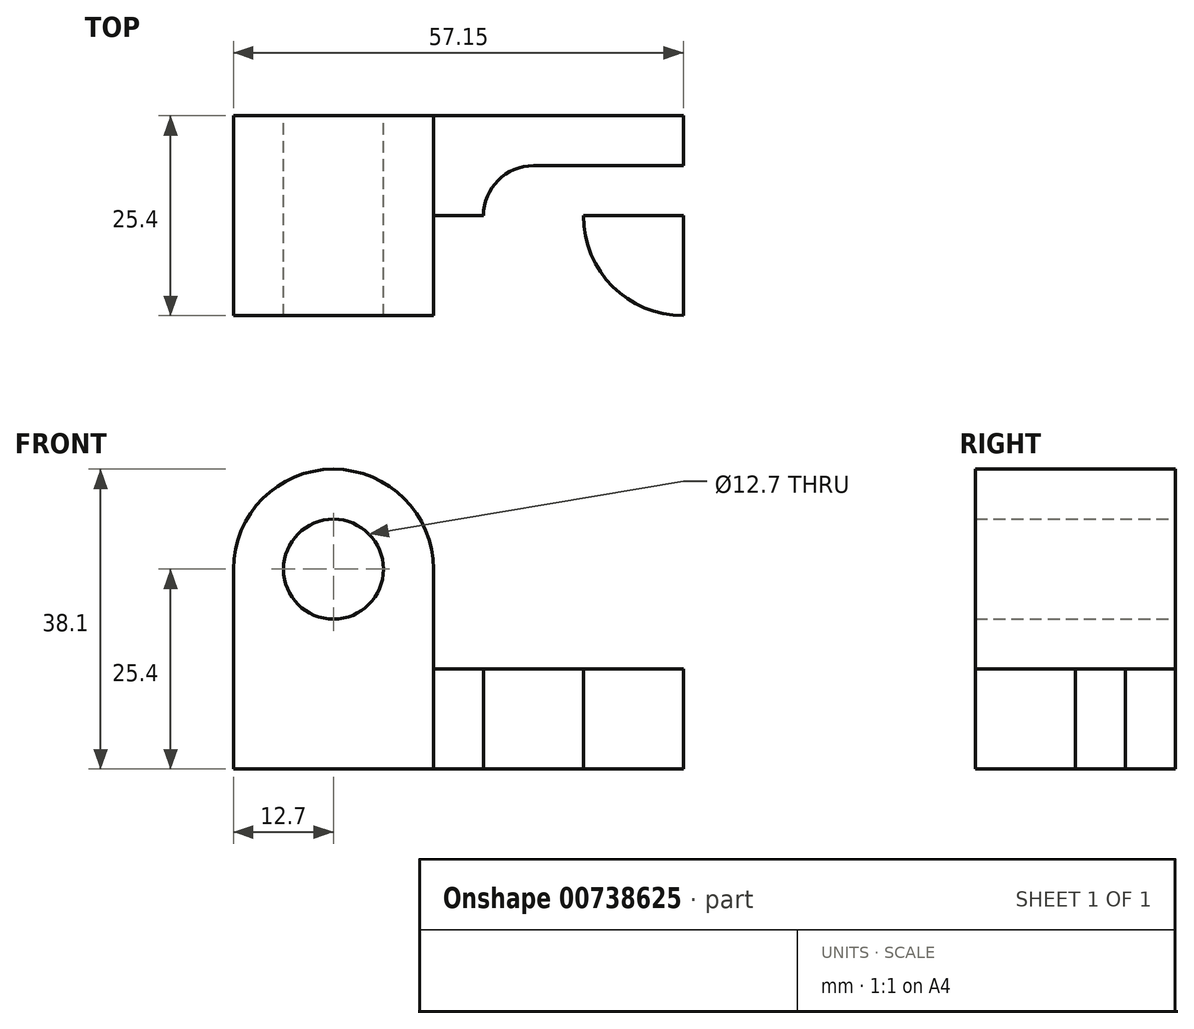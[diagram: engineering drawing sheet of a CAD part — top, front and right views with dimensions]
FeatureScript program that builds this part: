
annotation { "Feature Type Name" : "Feature", "Feature Type Description" : "" }
export const myFeature = defineFeature(function(context is Context, id is Id, definition is map)
    precondition{}
    {
        {
            var Q0;
            Q0=qCreatedBy(makeId("Front.planeOp"),FACE);
            var sketch = newSketch(context, id + "F0", { "sketchPlane" : qUnion([Q0])});
            skLineSegment(sketch, "E0", {"start": v(0, 25.4) * mm, "end": v(0, 0) * mm});
            skLineSegment(sketch, "E1", {"start": v(0, 0) * mm, "end": v(57.15, 0) * mm});
            skLineSegment(sketch, "E2", {"start": v(57.15, 0) * mm, "end": v(57.15, 12.7) * mm});
            skLineSegment(sketch, "E3", {"start": v(57.15, 0) * mm, "end": v(69.85, 0) * mm});
            skLineSegment(sketch, "E4", {"start": v(57.15, 12.7) * mm, "end": v(25.4, 12.7) * mm});
            skLineSegment(sketch, "E5", {"start": v(25.4, 12.7) * mm, "end": v(25.4, 25.4) * mm});
            skLineSegment(sketch, "E6", {"start": v(0, 25.4) * mm, "end": v(25.4, 25.4) * mm});
            skCircle(sketch, "E7", {"center": v(12.7, 25.4) * mm, "radius": 6.35 * mm});
            skCircle(sketch, "E8", {"center": v(12.7, 25.4) * mm, "radius": 12.7 * mm});
            skLineSegment(sketch, "E9.bottom", {"start": v(69.85, 0) * mm, "end": v(57.15, 0) * mm});
            skLineSegment(sketch, "E9.top", {"start": v(69.85, 12.7) * mm, "end": v(57.15, 12.7) * mm});
            skLineSegment(sketch, "E9.left", {"start": v(69.85, 0) * mm, "end": v(69.85, 12.7) * mm});
            skSolve(sketch);
        }
        {
            var Q0;
            Q0=makeQuery(id+"F0.imprint","IMPRINT",FACE,{"disambiguationData":[TD([[makeQuery(id+"F0.imprint","IMPRINT",EDGE,{"derivedFrom":sQuery(id+"F0.wireOp",EDGE,"E9.bottom")}),-1.0]])]});
            var Q1;
            {var subQ1=sQuery(id+"F0.wireOp",EDGE,"E0");Q1=makeQuery(id+"F0.imprint","IMPRINT",FACE,{"disambiguationData":[TD([[makeQuery(id+"F0.imprint","IMPRINT",EDGE,{"derivedFrom":subQ1}),1.0]])]});}
            var Q2;
            {var subQ1=sQuery(id+"F0.wireOp",EDGE,"E6");var subQ3=sQuery(id+"F0.wireOp",EDGE,"E7");var subQ4=makeQuery(id+"F0.imprint","INTERSECT",VERTEX,{"disambiguationData":[OD(0.0)],"derivedFrom":[subQ1,subQ3]});Q2=makeQuery(id+"F0.imprint","IMPRINT",FACE,{"disambiguationData":[TD([[makeQuery(id+"F0.imprint","IMPRINT",EDGE,{"disambiguationData":[TD([[subQ4,-1.0]])],"derivedFrom":subQ3}),-1.0]])]});}
            var Q3;
            {var subQ1=sQuery(id+"F0.wireOp",EDGE,"E6");var subQ3=sQuery(id+"F0.wireOp",EDGE,"E7");var subQ4=makeQuery(id+"F0.imprint","INTERSECT",VERTEX,{"disambiguationData":[OD(0.0)],"derivedFrom":[subQ1,subQ3]});Q3=makeQuery(id+"F0.imprint","IMPRINT",FACE,{"disambiguationData":[TD([[makeQuery(id+"F0.imprint","IMPRINT",EDGE,{"disambiguationData":[TD([[subQ4,1.0]])],"derivedFrom":subQ3}),-1.0]])]});}
            extrude(context, id + "F1", {"entities" : qUnion([Q0, Q1, Q2, Q3]), "depth" : 25.4 * mm, "offsetDistance" : 25.4 * mm});
        }
        {
            var Q0;
            Q0=makeQuery(id+"F1.opExtrude","SWEPT_FACE",FACE,{"disambiguationData":[OSD([sQuery(id+"F0.wireOp",EDGE,"E4"),sQuery(id+"F0.wireOp",EDGE,"E9.top")])]});
            var sketch = newSketch(context, id + "F2", { "sketchPlane" : qUnion([Q0])});
            skLineSegment(sketch, "E10", {"start": v(25.4, -12.7) * mm, "end": v(57.15, -12.7) * mm});
            skCircle(sketch, "E11", {"center": v(57.15, -12.7) * mm, "radius": 6.35 * mm});
            skCircle(sketch, "E12", {"center": v(57.15, -12.7) * mm, "radius": 12.7 * mm});
            skSolve(sketch);
        }
        {
            var Q0;
            {var subQ0=sQuery(id+"F2.wireOp",EDGE,"E12");var subQ1=sQuery(id+"F0.wireOp",EDGE,"E9.top");var subQ2=makeQuery(id+"F1.opExtrude","CAP_EDGE",EDGE,{"disambiguationData":[OSD([sQuery(id+"F0.wireOp",EDGE,"E4"),subQ1])],"isStart":true});var subQ3=makeQuery(id+"F2.imprint","INTERSECT",VERTEX,{"derivedFrom":[subQ2,subQ0]});Q0=makeQuery(id+"F2.imprint","IMPRINT",FACE,{"disambiguationData":[TD([[makeQuery(id+"F2.imprint","IMPRINT",EDGE,{"disambiguationData":[TD([[subQ3,1.0]])],"derivedFrom":subQ0}),-1.0]])]});}
            var Q1;
            {var subQ0=sQuery(id+"F2.wireOp",EDGE,"E12");var subQ1=sQuery(id+"F0.wireOp",EDGE,"E9.top");var subQ2=makeQuery(id+"F1.opExtrude","SWEPT_EDGE",EDGE,{"disambiguationData":[OSD([subQ1,sQuery(id+"F0.wireOp",EDGE,"E9.left")])]});var subQ3=makeQuery(id+"F2.imprint","INTERSECT",VERTEX,{"derivedFrom":[subQ2,subQ0]});Q1=makeQuery(id+"F2.imprint","IMPRINT",FACE,{"disambiguationData":[TD([[makeQuery(id+"F2.imprint","IMPRINT",EDGE,{"disambiguationData":[TD([[subQ3,1.0]])],"derivedFrom":subQ0}),-1.0]])]});}
            extrude(context, id + "F3", {"entities" : qUnion([Q0, Q1]), "operationType" : NewBodyOperationType.REMOVE, "endBound" : BoundingType.THROUGH_ALL, "oppositeDirection" : true, "depth" : 25.4 * mm, "offsetDistance" : 25.4 * mm});
        }
        {
            var Q0;
            Q0=makeQuery(id+"F1.opExtrude","SWEPT_FACE",FACE,{"disambiguationData":[OSD([sQuery(id+"F0.wireOp",EDGE,"E4"),sQuery(id+"F0.wireOp",EDGE,"E9.top")])]});
            var sketch = newSketch(context, id + "F4", { "sketchPlane" : qUnion([Q0])});
            skLineSegment(sketch, "E13", {"start": v(25.4, -12.7) * mm, "end": v(57.15, -12.7) * mm});
            skCircle(sketch, "E14", {"center": v(57.15, -12.7) * mm, "radius": 6.35 * mm});
            skLineSegment(sketch, "E15", {"start": v(25.4, -12.7) * mm, "end": v(38.1, -12.7) * mm});
            skCircle(sketch, "E16", {"center": v(38.1, -12.7) * mm, "radius": 6.35 * mm});
            skLineSegment(sketch, "E17", {"start": v(57.15, -12.7) * mm, "end": v(57.15, -6.35) * mm});
            skLineSegment(sketch, "E18", {"start": v(57.15, -12.7) * mm, "end": v(57.15, -19.05) * mm});
            skLineSegment(sketch, "E19", {"start": v(38.1, -12.7) * mm, "end": v(38.1, -19.05) * mm});
            skLineSegment(sketch, "E20", {"start": v(38.1, -12.7) * mm, "end": v(38.1, -6.35) * mm});
            skLineSegment(sketch, "E21", {"start": v(38.1, -6.35) * mm, "end": v(57.15, -6.35) * mm});
            skLineSegment(sketch, "E22", {"start": v(38.1, -19.05) * mm, "end": v(57.15, -19.05) * mm});
            skSolve(sketch);
        }
        {
            var Q0;
            {var subQ0=sQuery(id+"F4.wireOp",EDGE,"E20");Q0=makeQuery(id+"F4.imprint","IMPRINT",FACE,{"disambiguationData":[TD([[makeQuery(id+"F4.imprint","IMPRINT",EDGE,{"derivedFrom":subQ0}),1.0]])]});}
            var Q1;
            {var subQ0=sQuery(id+"F4.wireOp",EDGE,"E19");Q1=makeQuery(id+"F4.imprint","IMPRINT",FACE,{"disambiguationData":[TD([[makeQuery(id+"F4.imprint","IMPRINT",EDGE,{"derivedFrom":subQ0}),-1.0]])]});}
            var Q2;
            {var subQ0=sQuery(id+"F4.wireOp",EDGE,"E19");Q2=makeQuery(id+"F4.imprint","IMPRINT",FACE,{"disambiguationData":[TD([[makeQuery(id+"F4.imprint","IMPRINT",EDGE,{"derivedFrom":subQ0}),1.0]])]});}
            var Q3;
            {var subQ0=sQuery(id+"F4.wireOp",EDGE,"E20");Q3=makeQuery(id+"F4.imprint","IMPRINT",FACE,{"disambiguationData":[TD([[makeQuery(id+"F4.imprint","IMPRINT",EDGE,{"derivedFrom":subQ0}),-1.0]])]});}
            var Q4;
            {var subQ5=sQuery(id+"F4.wireOp",EDGE,"E21");Q4=makeQuery(id+"F4.imprint","IMPRINT",FACE,{"disambiguationData":[TD([[makeQuery(id+"F4.imprint","IMPRINT",EDGE,{"derivedFrom":subQ5}),-1.0]])]});}
            var Q5;
            {var subQ0=sQuery(id+"F4.wireOp",EDGE,"E17");Q5=makeQuery(id+"F4.imprint","IMPRINT",FACE,{"disambiguationData":[TD([[makeQuery(id+"F4.imprint","IMPRINT",EDGE,{"derivedFrom":subQ0}),1.0]])]});}
            var Q6;
            {var subQ0=sQuery(id+"F4.wireOp",EDGE,"E17");Q6=makeQuery(id+"F4.imprint","IMPRINT",FACE,{"disambiguationData":[TD([[makeQuery(id+"F4.imprint","IMPRINT",EDGE,{"derivedFrom":subQ0}),-1.0]])]});}
            var Q7;
            {var subQ0=sQuery(id+"F4.wireOp",EDGE,"E18");Q7=makeQuery(id+"F4.imprint","IMPRINT",FACE,{"disambiguationData":[TD([[makeQuery(id+"F4.imprint","IMPRINT",EDGE,{"derivedFrom":subQ0}),-1.0]])]});}
            var Q8;
            {var subQ5=sQuery(id+"F4.wireOp",EDGE,"E22");Q8=makeQuery(id+"F4.imprint","IMPRINT",FACE,{"disambiguationData":[TD([[makeQuery(id+"F4.imprint","IMPRINT",EDGE,{"derivedFrom":subQ5}),1.0]])]});}
            extrude(context, id + "F5", {"entities" : qUnion([Q0, Q1, Q2, Q3, Q4, Q5, Q6, Q7, Q8]), "operationType" : NewBodyOperationType.REMOVE, "endBound" : BoundingType.THROUGH_ALL, "oppositeDirection" : true, "depth" : 25.4 * mm, "offsetDistance" : 25.4 * mm});
        }
    });
